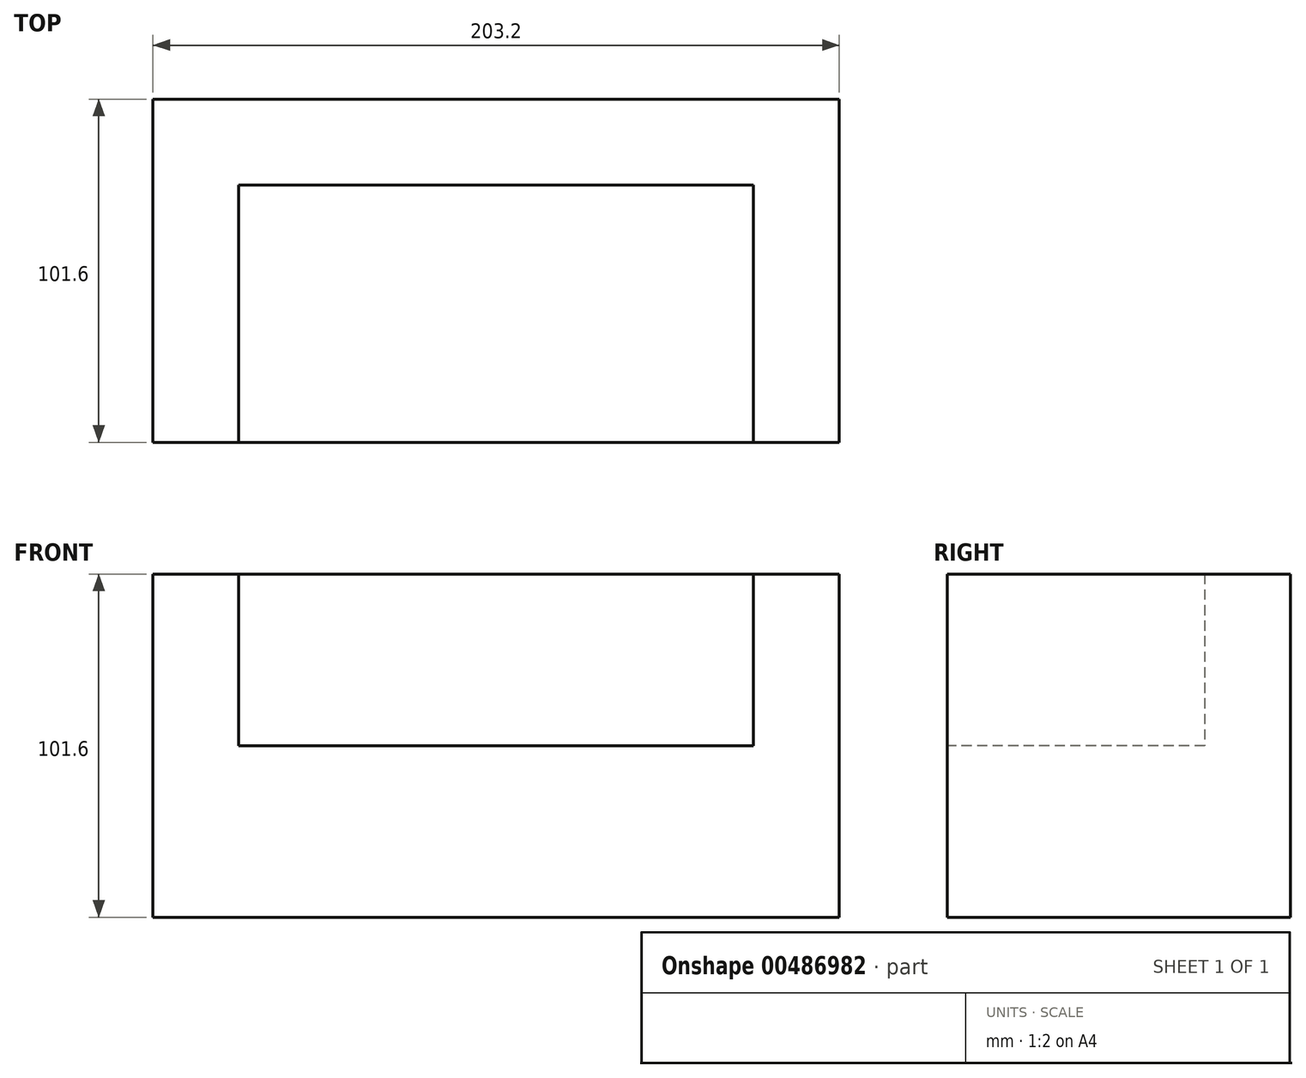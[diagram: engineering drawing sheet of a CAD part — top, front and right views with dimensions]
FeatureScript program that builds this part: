
annotation { "Feature Type Name" : "Feature", "Feature Type Description" : "" }
export const myFeature = defineFeature(function(context is Context, id is Id, definition is map)
    precondition{}
    {
        {
            var Q0;
            Q0=qCreatedBy(makeId("Front.planeOp"),FACE);
            var sketch = newSketch(context, id + "F0", { "sketchPlane" : qUnion([Q0])});
            skLineSegment(sketch, "E0.bottom", {"start": v(-89.36, 43.13) * mm, "end": v(88.44, 43.13) * mm});
            skLineSegment(sketch, "E0.top", {"start": v(-89.36, -58.47) * mm, "end": v(88.44, -58.47) * mm});
            skLineSegment(sketch, "E0.left", {"start": v(-89.36, 43.13) * mm, "end": v(-89.36, -58.47) * mm});
            skLineSegment(sketch, "E0.right", {"start": v(88.44, 43.13) * mm, "end": v(88.44, -58.47) * mm});
            skSolve(sketch);
        }
        {
            var Q0;
            Q0=makeQuery(id+"F0.imprint","IMPRINT",FACE,{"disambiguationData":[TD([[makeQuery(id+"F0.imprint","IMPRINT",EDGE,{"derivedFrom":sQuery(id+"F0.wireOp",EDGE,"E0.bottom")}),-1.0]])]});
            var Q1;
            Q1 = qSketchRegion(id + "F0", true);
            extrude(context, id + "F1", {"entities" : qUnion([Q0, Q1]), "depth" : 101.6 * mm});
        }
        {
            var Q0;
            Q0=makeQuery(id+"F1.opExtrude","CAP_FACE",FACE,{"disambiguationData":[OSD([sQuery(id+"F0.wireOp",EDGE,"E0.bottom"),sQuery(id+"F0.wireOp",EDGE,"E0.top"),sQuery(id+"F0.wireOp",EDGE,"E0.left"),sQuery(id+"F0.wireOp",EDGE,"E0.right")])],"isStart":false});
            var sketch = newSketch(context, id + "F2", { "sketchPlane" : qUnion([Q0])});
            skLineSegment(sketch, "E1.bottom", {"start": v(-89.36, 43.13) * mm, "end": v(63.04, 43.13) * mm});
            skLineSegment(sketch, "E1.top", {"start": v(-89.36, -7.67) * mm, "end": v(63.04, -7.67) * mm});
            skLineSegment(sketch, "E1.left", {"start": v(-89.36, 43.13) * mm, "end": v(-89.36, -7.67) * mm});
            skLineSegment(sketch, "E1.right", {"start": v(63.04, 43.13) * mm, "end": v(63.04, -7.67) * mm});
            skSolve(sketch);
        }
        {
            var Q0;
            Q0 = qSketchRegion(id + "F2", true);
            extrude(context, id + "F3", {"entities" : qUnion([Q0]), "operationType" : NewBodyOperationType.REMOVE, "oppositeDirection" : true, "depth" : 76.2 * mm});
        }
        {
            var Q0;
            Q0=makeQuery(id+"F1.opExtrude","CAP_FACE",FACE,{"disambiguationData":[OSD([sQuery(id+"F0.wireOp",EDGE,"E0.bottom"),sQuery(id+"F0.wireOp",EDGE,"E0.top"),sQuery(id+"F0.wireOp",EDGE,"E0.left"),sQuery(id+"F0.wireOp",EDGE,"E0.right")])],"isStart":false});
            var sketch = newSketch(context, id + "F4", { "sketchPlane" : qUnion([Q0])});
            skLineSegment(sketch, "E2.bottom", {"start": v(-89.36, -58.47) * mm, "end": v(-114.76, -58.47) * mm});
            skLineSegment(sketch, "E2.top", {"start": v(-89.36, 43.13) * mm, "end": v(-114.76, 43.13) * mm});
            skLineSegment(sketch, "E2.left", {"start": v(-89.36, -58.47) * mm, "end": v(-89.36, 43.13) * mm});
            skLineSegment(sketch, "E2.right", {"start": v(-114.76, -58.47) * mm, "end": v(-114.76, 43.13) * mm});
            skSolve(sketch);
        }
        {
            var Q0;
            Q0 = qSketchRegion(id + "F4", true);
            extrude(context, id + "F5", {"entities" : qUnion([Q0]), "operationType" : NewBodyOperationType.ADD, "oppositeDirection" : true, "depth" : 101.6 * mm});
        }
    });
